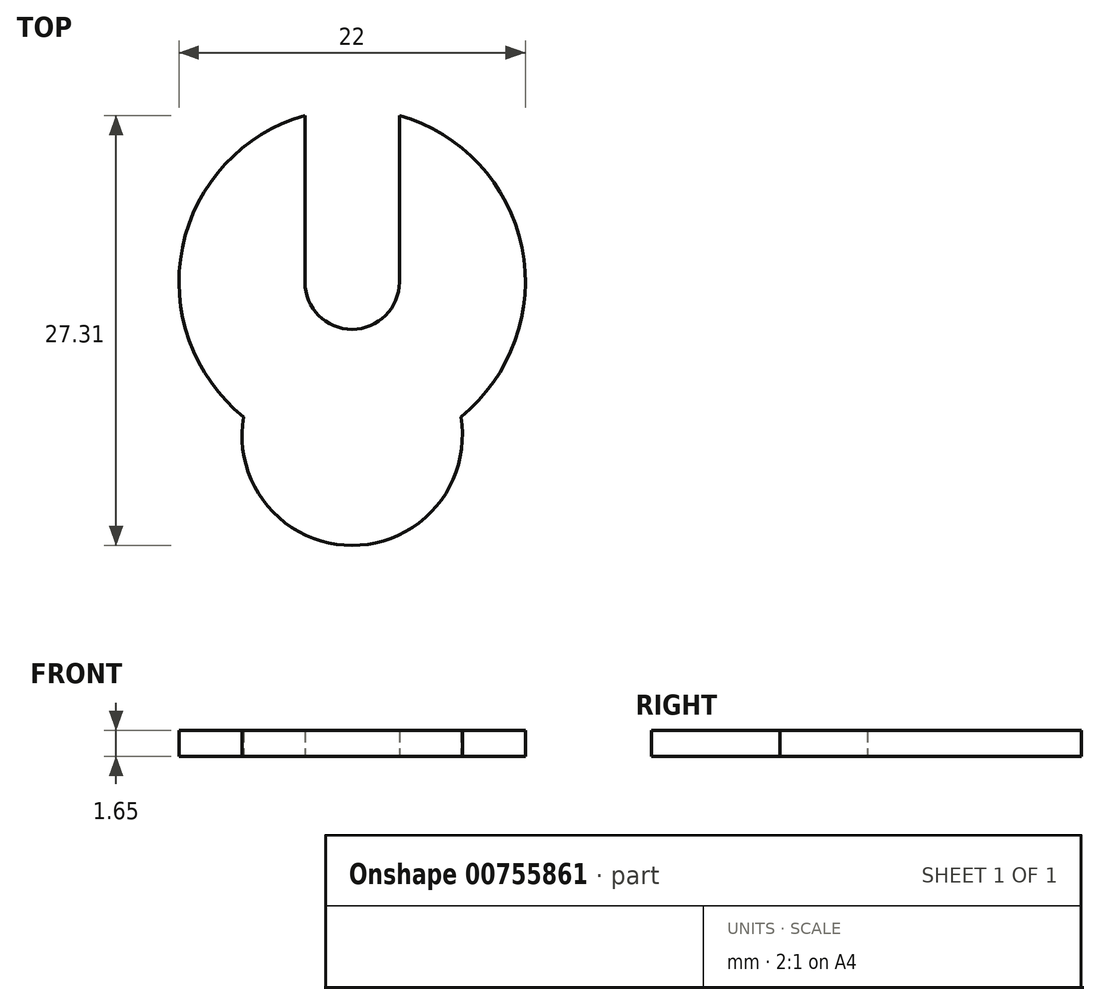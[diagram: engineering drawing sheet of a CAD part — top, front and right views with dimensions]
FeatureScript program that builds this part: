
annotation { "Feature Type Name" : "Feature", "Feature Type Description" : "" }
export const myFeature = defineFeature(function(context is Context, id is Id, definition is map)
    precondition{}
    {
        {
            var Q0;
            Q0=qCreatedBy(makeId("Top.planeOp"),FACE);
            var sketch = newSketch(context, id + "F0", { "sketchPlane" : qUnion([Q0])});
            skArc(sketch, "E0", {"start": v(-3, 10.58) * mm, "mid": v(0, -11) * mm, "end": v(3, 10.58) * mm});
            skArc(sketch, "E1", {"start": v(-3, 0) * mm, "mid": v(0, -3) * mm, "end": v(3, 0) * mm});
            skLineSegment(sketch, "E2.left", {"start": v(-3, 0) * mm, "end": v(-3, 10.58) * mm});
            skLineSegment(sketch, "E2.right", {"start": v(3, 0) * mm, "end": v(3, 10.58) * mm});
            skArc(sketch, "E3", {"start": v(-6.9, -8.57) * mm, "mid": v(0, -16.73) * mm, "end": v(6.9, -8.57) * mm});
            skLineSegment(sketch, "E4", {"start": v(-6.9, -8.57) * mm, "end": v(6.9, -8.57) * mm, "construction": true});
            skSolve(sketch);
        }
        {
            var Q0;
            Q0 = qSketchRegion(id + "F0", true);
            extrude(context, id + "F1", {"entities" : qUnion([Q0]), "depth" : 1.65 * mm, "offsetDistance" : 25 * mm});
        }
    });
